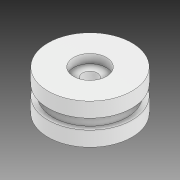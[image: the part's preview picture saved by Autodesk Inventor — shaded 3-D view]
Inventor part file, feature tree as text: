
AUTODESK INVENTOR PART (.ipt)
format: ipt  version: 2020 (Build 240168000, 168)  size: 158,208 bytes
history: native  units: mm
features: sketch x3, extrude x2, revolve x1
ambient origin geometry x8: Origin, YZ Plane, XZ Plane, XY Plane, X Axis, Y Axis, Z Axis, Center Point
bodies: Solid1 (feature_tree)
feature tree (6):
  revolve  "Revolution1"  [1 undecoded]
  extrude  "Extrusion1"  TaperAngle=90.0deg  [1 undecoded]
  extrude  "Extrusion2"  Depth=6.0mm TaperAngle=0.0deg
  sketch  "Sketch1"  dims[d1=3.3mm d2=7.0mm]
  sketch  "Sketch2"  dims[d4=10.0mm d5=90.0deg]
  sketch  "Sketch3"  dims[d8=22.3mm d9=6.0mm d10=0.0mm d11=22.3mm d12=6.0mm d13=0.0mm d15=25.0mm d16=5.0mm]
note: 2 required parameter values undecoded (feature->parameter linkage not recoverable at this tier; creation-order binding heuristic only, values carry confidence <= 0.55)